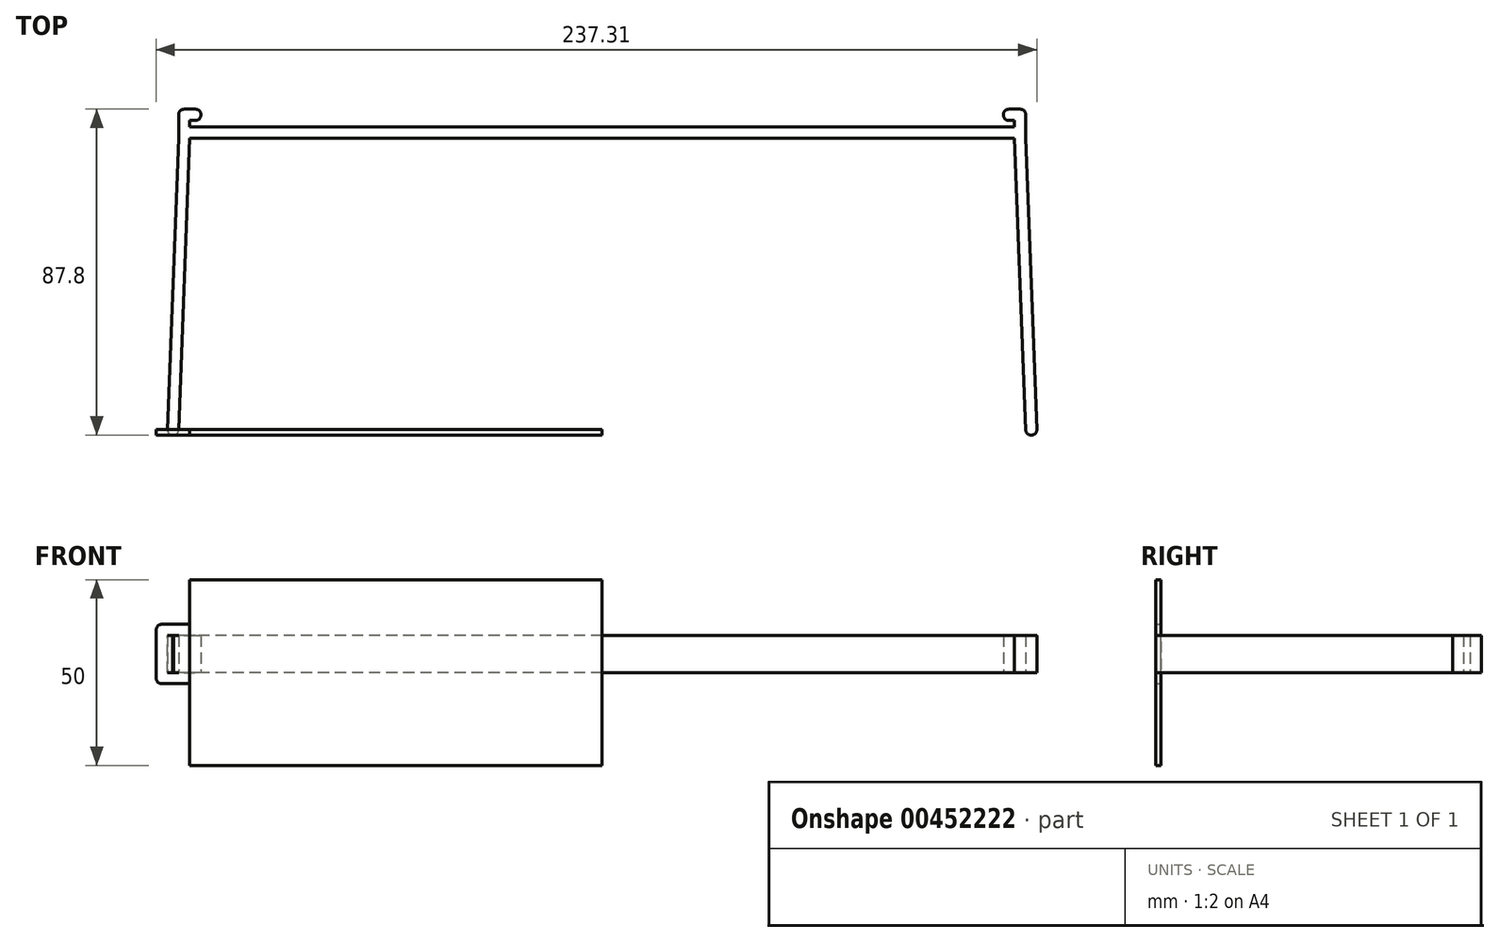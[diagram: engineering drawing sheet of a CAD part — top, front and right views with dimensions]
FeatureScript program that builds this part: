
annotation { "Feature Type Name" : "Feature", "Feature Type Description" : "" }
export const myFeature = defineFeature(function(context is Context, id is Id, definition is map)
    precondition{}
    {
        {
            assignVariable(context, id + "F0", {"name" : "Thickness", "anyValue" : 3});
        }
        {
            assignVariable(context, id + "F1", {"name" : "Depth", "anyValue" : 10});
        }
        {
            var Q0;
            Q0=qCreatedBy(makeId("Top.planeOp"),FACE);
            var sketch = newSketch(context, id + "F2", { "sketchPlane" : qUnion([Q0])});
            skLineSegment(sketch, "E0.bottom", {"start": v(0, 0) * mm, "end": v(-111.12, 0) * mm});
            skLineSegment(sketch, "E0.top", {"start": v(0, 3) * mm, "end": v(-111.12, 3) * mm});
            skLineSegment(sketch, "E0.left", {"start": v(0, 0) * mm, "end": v(0, 3) * mm});
            skLineSegment(sketch, "E0.right", {"start": v(-111.12, 0) * mm, "end": v(-111.12, 3) * mm});
            skLineSegment(sketch, "E1", {"start": v(-111.12, 0) * mm, "end": v(-114.12, 0) * mm});
            skLineSegment(sketch, "E2", {"start": v(-114.12, 0) * mm, "end": v(-114.12, 7.8) * mm});
            skLineSegment(sketch, "E3", {"start": v(-114.12, 7.8) * mm, "end": v(-108.12, 7.8) * mm});
            skLineSegment(sketch, "E4", {"start": v(-108.12, 7.8) * mm, "end": v(-108.12, 4.8) * mm});
            skLineSegment(sketch, "E5", {"start": v(-108.12, 4.8) * mm, "end": v(-111.12, 4.8) * mm});
            skLineSegment(sketch, "E6", {"start": v(-111.12, 4.8) * mm, "end": v(-111.12, 3) * mm});
            skLineSegment(sketch, "E7.bottom", {"start": v(0, -78.5) * mm, "end": v(-111.12, -78.5) * mm});
            skLineSegment(sketch, "E7.top", {"start": v(0, -80) * mm, "end": v(-111.12, -80) * mm});
            skLineSegment(sketch, "E7.left", {"start": v(0, -80) * mm, "end": v(0, -78.5) * mm});
            skLineSegment(sketch, "E7.right", {"start": v(-111.12, -80) * mm, "end": v(-111.12, -78.5) * mm});
            skLineSegment(sketch, "E8", {"start": v(-102.07, -80) * mm, "end": v(-111.12, -80) * mm, "construction": true});
            skLineSegment(sketch, "E9", {"start": v(-111.12, 0) * mm, "end": v(-114.18, -80) * mm});
            skLineSegment(sketch, "E10", {"start": v(-114.18, -80) * mm, "end": v(-117.18, -80) * mm});
            skLineSegment(sketch, "E11", {"start": v(-117.18, -80) * mm, "end": v(-114.12, 0) * mm});
            skSolve(sketch);
        }
        {
            var Q0;
            Q0=makeQuery(id+"F2.imprint","IMPRINT",FACE,{"disambiguationData":[TD([[makeQuery(id+"F2.imprint","IMPRINT",EDGE,{"derivedFrom":sQuery(id+"F2.wireOp",EDGE,"E1")}),1.0]])]});
            var Q1;
            Q1=makeQuery(id+"F2.imprint","IMPRINT",FACE,{"disambiguationData":[TD([[makeQuery(id+"F2.imprint","IMPRINT",EDGE,{"derivedFrom":sQuery(id+"F2.wireOp",EDGE,"E0.right")}),1.0]])]});
            var Q2;
            Q2=makeQuery(id+"F2.imprint","IMPRINT",FACE,{"disambiguationData":[TD([[makeQuery(id+"F2.imprint","IMPRINT",EDGE,{"derivedFrom":sQuery(id+"F2.wireOp",EDGE,"E0.bottom")}),-1.0]])]});
            extrude(context, id + "F3", {"entities" : qUnion([Q0, Q1, Q2]), "depth" : (getVariable(context, 'Depth')) * mm});
        }
        {
            var Q0;
            Q0=makeQuery(id+"F3.opExtrude","SWEPT_EDGE",EDGE,{"disambiguationData":[OSD([sQuery(id+"F2.wireOp",EDGE,"E10"),sQuery(id+"F2.wireOp",EDGE,"E11")])]});
            var Q1;
            Q1=makeQuery(id+"F3.opExtrude","SWEPT_EDGE",EDGE,{"disambiguationData":[OSD([sQuery(id+"F2.wireOp",EDGE,"E9"),sQuery(id+"F2.wireOp",EDGE,"E10")])]});
            var Q2;
            Q2=makeQuery(id+"F3.opExtrude","SWEPT_EDGE",EDGE,{"disambiguationData":[OSD([sQuery(id+"F2.wireOp",EDGE,"E3"),sQuery(id+"F2.wireOp",EDGE,"E4")])]});
            var Q3;
            Q3=makeQuery(id+"F3.opExtrude","SWEPT_EDGE",EDGE,{"disambiguationData":[OSD([sQuery(id+"F2.wireOp",EDGE,"E4"),sQuery(id+"F2.wireOp",EDGE,"E5")])]});
            var Q4;
            Q4=makeQuery(id+"F3.opExtrude","SWEPT_EDGE",EDGE,{"disambiguationData":[OSD([sQuery(id+"F2.wireOp",EDGE,"E2"),sQuery(id+"F2.wireOp",EDGE,"E3")])]});
            fillet(context, id + "F4", {"entities" : qUnion([Q0, Q1, Q2, Q3, Q4]), "radius" : (getVariable(context, 'Thickness') / 2 - 0.1) * mm, "tangentPropagation" : true, "allowEdgeOverflow" : false});
        }
        {
            var Q0;
            Q0=makeQuery(id+"F3.opExtrude","SWEPT_BODY",BODY,{"disambiguationData":[OSD([sQuery(id+"F2.wireOp",EDGE,"E0.bottom"),sQuery(id+"F2.wireOp",EDGE,"E0.top"),sQuery(id+"F2.wireOp",EDGE,"E0.left"),sQuery(id+"F2.wireOp",EDGE,"E2"),sQuery(id+"F2.wireOp",EDGE,"E3"),sQuery(id+"F2.wireOp",EDGE,"E4"),sQuery(id+"F2.wireOp",EDGE,"E5"),sQuery(id+"F2.wireOp",EDGE,"E6"),sQuery(id+"F2.wireOp",EDGE,"E9"),sQuery(id+"F2.wireOp",EDGE,"E10"),sQuery(id+"F2.wireOp",EDGE,"E11")])]});
            var Q1;
            Q1=makeQuery(id+"F3.opExtrude","SWEPT_FACE",FACE,{"disambiguationData":[OSD([sQuery(id+"F2.wireOp",EDGE,"E0.left")])]});
            mirror(context, id + "F5", {"operationType" : NewBodyOperationType.ADD, "entities" : qUnion([Q0]), "mirrorPlane" : qUnion([Q1])});
        }
        {
            var Q0;
            Q0=makeQuery(id+"F2.imprint","IMPRINT",FACE,{"disambiguationData":[TD([[makeQuery(id+"F2.imprint","IMPRINT",EDGE,{"derivedFrom":sQuery(id+"F2.wireOp",EDGE,"E7.bottom")}),1.0]])]});
            extrude(context, id + "F6", {"entities" : qUnion([Q0]), "endBound" : BoundingType.SYMMETRIC, "depth" : 50 * mm});
        }
        {
            var Q0;
            Q0=makeQuery(id+"F6.opExtrude","SWEPT_FACE",FACE,{"disambiguationData":[OSD([sQuery(id+"F2.wireOp",EDGE,"E7.bottom")])]});
            var sketch = newSketch(context, id + "F7", { "sketchPlane" : qUnion([Q0])});
            skLineSegment(sketch, "E12.0", {"start": v(117.13, 10) * mm, "end": v(114.12, 10) * mm});
            skLineSegment(sketch, "E13.0", {"start": v(111.12, 10) * mm, "end": v(114.13, 10) * mm});
            skLineSegment(sketch, "E14.0", {"start": v(117.18, 0) * mm, "end": v(114.12, 0) * mm});
            skLineSegment(sketch, "E15.0", {"start": v(111.12, 0) * mm, "end": v(114.18, 0) * mm});
            skLineSegment(sketch, "E16.bottom", {"start": v(117.18, 0) * mm, "end": v(111.12, 0) * mm});
            skLineSegment(sketch, "E16.top", {"start": v(117.18, 10) * mm, "end": v(111.12, 10) * mm});
            skLineSegment(sketch, "E16.left", {"start": v(117.18, 0) * mm, "end": v(117.18, 10) * mm});
            skLineSegment(sketch, "E16.right", {"start": v(111.12, 0) * mm, "end": v(111.12, 10) * mm});
            skLineSegment(sketch, "E17.0", {"start": v(120.18, -3) * mm, "end": v(111.12, -3) * mm});
            skLineSegment(sketch, "E17.1", {"start": v(120.18, -3) * mm, "end": v(120.18, 13) * mm});
            skLineSegment(sketch, "E17.2", {"start": v(120.18, 13) * mm, "end": v(111.12, 13) * mm});
            skSolve(sketch);
        }
        {
            var Q0;
            {var subQ1=sQuery(id+"F7.wireOp",EDGE,"E16.left");Q0=makeQuery(id+"F7.imprint","IMPRINT",FACE,{"disambiguationData":[TD([[makeQuery(id+"F7.imprint","IMPRINT",EDGE,{"derivedFrom":subQ1}),-1.0]])]});}
            var Q1;
            {var subQ0=sQuery(id+"F7.wireOp",EDGE,"E16.left");Q1=makeQuery(id+"F7.imprint","IMPRINT",FACE,{"disambiguationData":[TD([[makeQuery(id+"F7.imprint","IMPRINT",EDGE,{"derivedFrom":subQ0}),1.0]])]});}
            var Q2;
            Q2=makeQuery(id+"F6.opExtrude","SWEPT_FACE",FACE,{"disambiguationData":[OSD([sQuery(id+"F2.wireOp",EDGE,"E7.top")])]});
            extrude(context, id + "F8", {"entities" : qUnion([Q0, Q1]), "endBound" : BoundingType.UP_TO_SURFACE, "oppositeDirection" : true, "endBoundEntityFace" : qUnion([Q2]), "depth" : 25 * mm});
        }
        {
            var Q0;
            Q0=makeQuery(id+"F3.opExtrude","SWEPT_BODY",BODY,{"disambiguationData":[OSD([sQuery(id+"F2.wireOp",EDGE,"E0.bottom"),sQuery(id+"F2.wireOp",EDGE,"E0.top"),sQuery(id+"F2.wireOp",EDGE,"E0.left"),sQuery(id+"F2.wireOp",EDGE,"E2"),sQuery(id+"F2.wireOp",EDGE,"E3"),sQuery(id+"F2.wireOp",EDGE,"E4"),sQuery(id+"F2.wireOp",EDGE,"E5"),sQuery(id+"F2.wireOp",EDGE,"E6"),sQuery(id+"F2.wireOp",EDGE,"E9"),sQuery(id+"F2.wireOp",EDGE,"E10"),sQuery(id+"F2.wireOp",EDGE,"E11")])]});
            var Q1;
            Q1=makeQuery(id+"F8.opExtrude","SWEPT_BODY",BODY,{"disambiguationData":[OSD([sQuery(id+"F2.wireOp",EDGE,"E7.bottom"),sQuery(id+"F2.wireOp",EDGE,"E7.right"),sQuery(id+"F7.wireOp",EDGE,"E16.right"),sQuery(id+"F7.wireOp",EDGE,"E17.0"),sQuery(id+"F7.wireOp",EDGE,"E17.1"),sQuery(id+"F7.wireOp",EDGE,"E17.2")])]});
            booleanBodies(context, id + "F9", {"operationType" : BooleanOperationType.SUBTRACTION, "tools" : qUnion([Q0]), "targets" : qUnion([Q1]), "keepTools" : true});
        }
        {
            var Q0;
            Q0=makeQuery(id+"F8.opExtrude","SWEPT_EDGE",EDGE,{"disambiguationData":[OSD([sQuery(id+"F7.wireOp",EDGE,"E17.1"),sQuery(id+"F7.wireOp",EDGE,"E17.2")])]});
            var Q1;
            Q1=makeQuery(id+"F8.opExtrude","SWEPT_EDGE",EDGE,{"disambiguationData":[OSD([sQuery(id+"F7.wireOp",EDGE,"E17.0"),sQuery(id+"F7.wireOp",EDGE,"E17.1")])]});
            fillet(context, id + "F10", {"entities" : qUnion([Q0, Q1]), "radius" : (getVariable(context, 'Thickness') / 2) * mm, "tangentPropagation" : true, "allowEdgeOverflow" : false});
        }
    });
